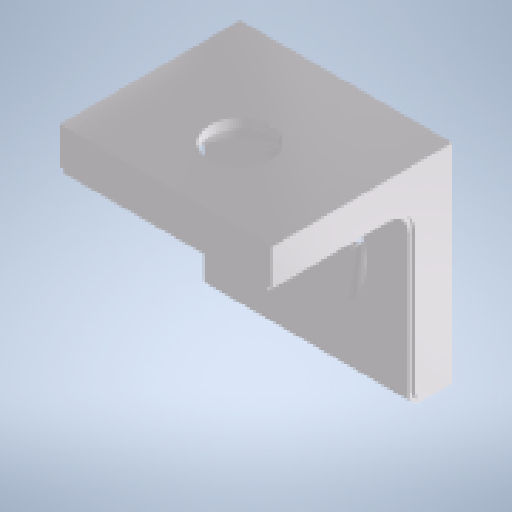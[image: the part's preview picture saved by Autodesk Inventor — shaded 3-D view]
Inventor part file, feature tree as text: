
AUTODESK INVENTOR PART (.ipt)
format: ipt  version: 2025 (Build 290162010, 162A)  size: 189,440 bytes
history: native  units: mm
features: extrude x1, sketch x1, other x1
ambient origin geometry x8: Origin, YZ Plane, XZ Plane, XY Plane, X Axis, Y Axis, Z Axis, Center Point
bodies: Volumenkörper1 (feature_tree)
feature tree (3):
  extrude  "Extrusion1"  [1 undecoded]
  sketch  "Skizze1"  dims[d0=3.0mm d1=0.0mm]
  other  "item_67777_winkel-5-20-weissalumini__high_1_1:1"
note: 1 required parameter value undecoded (feature->parameter linkage not recoverable at this tier; creation-order binding heuristic only, values carry confidence <= 0.55)
